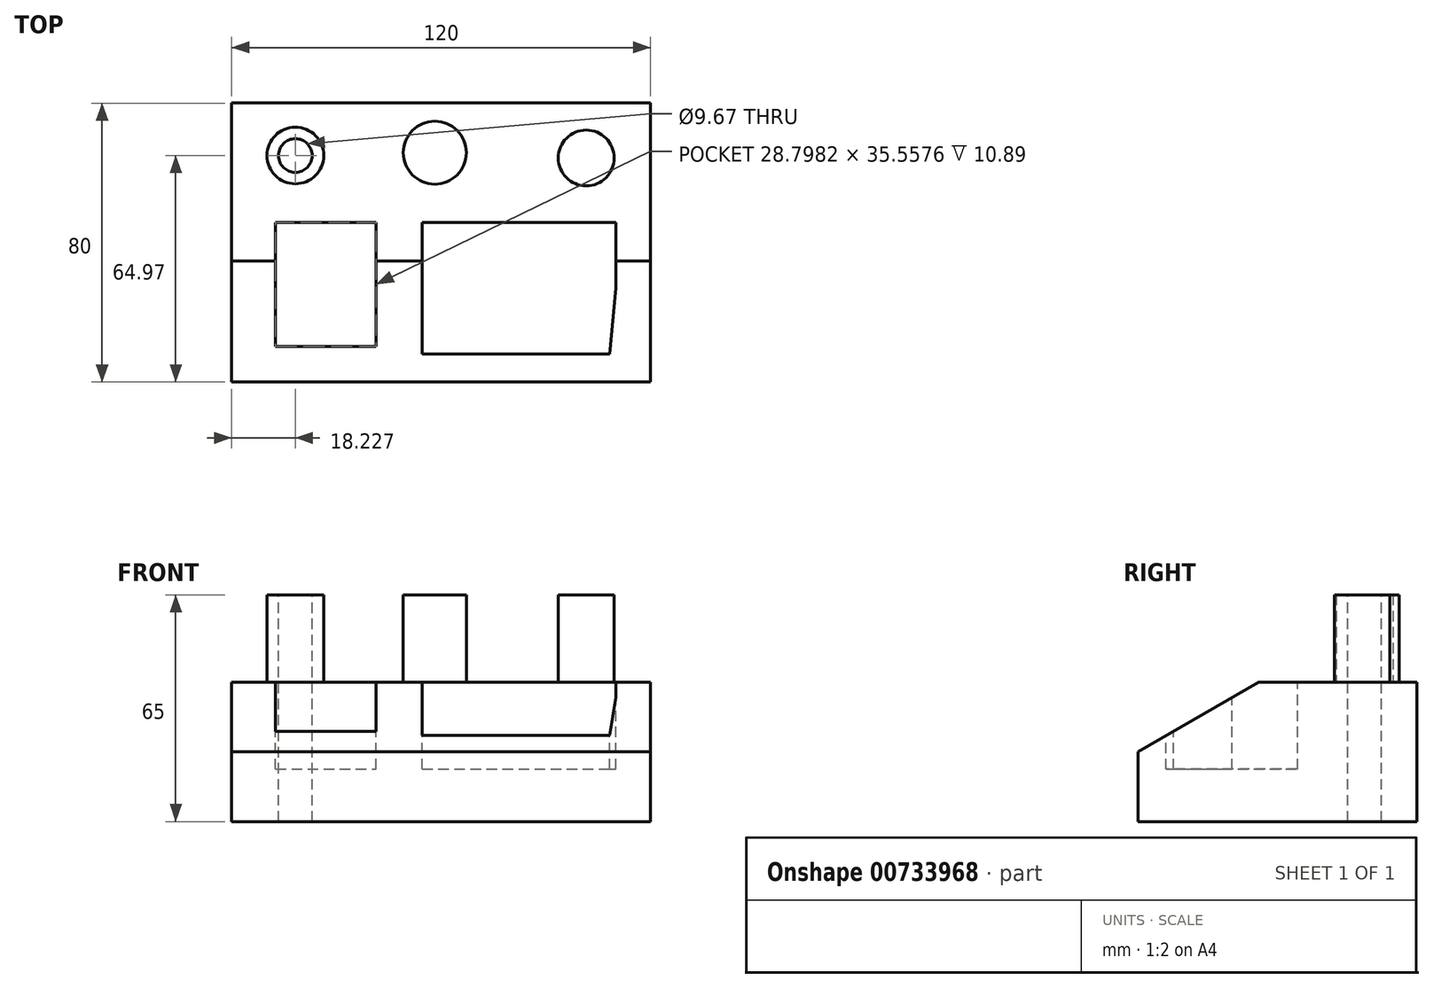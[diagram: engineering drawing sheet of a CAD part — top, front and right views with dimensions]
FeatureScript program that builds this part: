
annotation { "Feature Type Name" : "Feature", "Feature Type Description" : "" }
export const myFeature = defineFeature(function(context is Context, id is Id, definition is map)
    precondition{}
    {
        {
            var Q0;
            Q0=qCreatedBy(makeId("Top.planeOp"),FACE);
            var sketch = newSketch(context, id + "F0", { "sketchPlane" : qUnion([Q0])});
            skLineSegment(sketch, "E0.bottom", {"start": v(-64.23, 34.23) * mm, "end": v(55.77, 34.23) * mm});
            skLineSegment(sketch, "E0.top", {"start": v(-64.23, -45.77) * mm, "end": v(55.77, -45.77) * mm});
            skLineSegment(sketch, "E0.left", {"start": v(-64.23, 34.23) * mm, "end": v(-64.23, -45.77) * mm});
            skLineSegment(sketch, "E0.right", {"start": v(55.77, 34.23) * mm, "end": v(55.77, -45.77) * mm});
            skSolve(sketch);
        }
        {
            var Q0;
            Q0 = qSketchRegion(id + "F0", true);
            extrude(context, id + "F1", {"entities" : qUnion([Q0]), "depth" : 40 * mm, "offsetDistance" : 25 * mm});
        }
        {
            var Q0;
            Q0=makeQuery(id+"F1.opExtrude","CAP_FACE",FACE,{"disambiguationData":[OSD([sQuery(id+"F0.wireOp",EDGE,"E0.bottom"),sQuery(id+"F0.wireOp",EDGE,"E0.top"),sQuery(id+"F0.wireOp",EDGE,"E0.left"),sQuery(id+"F0.wireOp",EDGE,"E0.right")])],"isStart":false});
            var sketch = newSketch(context, id + "F2", { "sketchPlane" : qUnion([Q0])});
            skLineSegment(sketch, "E1.bottom", {"start": v(-51.66, -35.56) * mm, "end": v(-22.86, -35.56) * mm});
            skLineSegment(sketch, "E1.top", {"start": v(-51.66, 0) * mm, "end": v(-22.86, 0) * mm});
            skLineSegment(sketch, "E1.left", {"start": v(-51.66, -35.56) * mm, "end": v(-51.66, 0) * mm});
            skLineSegment(sketch, "E1.right", {"start": v(-22.86, -35.56) * mm, "end": v(-22.86, 0) * mm});
            skLineSegment(sketch, "E2.bottom", {"start": v(-9.64, 0) * mm, "end": v(45.77, 0) * mm});
            skLineSegment(sketch, "E2.left", {"start": v(-9.64, 0) * mm, "end": v(-9.64, -37.68) * mm});
            skLineSegment(sketch, "E2.right", {"start": v(45.77, 0) * mm, "end": v(45.77, -18.74) * mm});
            skLineSegment(sketch, "E3", {"start": v(-9.64, -37.68) * mm, "end": v(44.11, -37.68) * mm});
            skLineSegment(sketch, "E4", {"start": v(44.11, -37.68) * mm, "end": v(45.77, -18.74) * mm});
            skSolve(sketch);
        }
        {
            var Q0;
            Q0 = qSketchRegion(id + "F2", true);
            extrude(context, id + "F3", {"entities" : qUnion([Q0]), "operationType" : NewBodyOperationType.REMOVE, "oppositeDirection" : true, "depth" : 25 * mm, "offsetDistance" : 25 * mm});
        }
        {
            var Q0;
            Q0=makeQuery(id+"F1.opExtrude","SWEPT_FACE",FACE,{"disambiguationData":[OSD([sQuery(id+"F0.wireOp",EDGE,"E0.right")])]});
            var sketch = newSketch(context, id + "F4", { "sketchPlane" : qUnion([Q0])});
            skLineSegment(sketch, "E5", {"start": v(-45.77, 20) * mm, "end": v(-11.1, 40) * mm});
            skLineSegment(sketch, "E6", {"start": v(-11.1, 40) * mm, "end": v(-45.77, 40) * mm});
            skLineSegment(sketch, "E7", {"start": v(-45.77, 40) * mm, "end": v(-45.77, 20) * mm});
            skSolve(sketch);
        }
        {
            var Q0;
            Q0 = qSketchRegion(id + "F4", true);
            extrude(context, id + "F5", {"entities" : qUnion([Q0]), "operationType" : NewBodyOperationType.REMOVE, "endBound" : BoundingType.THROUGH_ALL, "oppositeDirection" : true, "depth" : 25 * mm, "offsetDistance" : 25 * mm});
        }
        {
            var Q0;
            Q0=makeQuery(id+"F1.opExtrude","CAP_FACE",FACE,{"disambiguationData":[OSD([sQuery(id+"F0.wireOp",EDGE,"E0.bottom"),sQuery(id+"F0.wireOp",EDGE,"E0.top"),sQuery(id+"F0.wireOp",EDGE,"E0.left"),sQuery(id+"F0.wireOp",EDGE,"E0.right")])],"isStart":false});
            var sketch = newSketch(context, id + "F6", { "sketchPlane" : qUnion([Q0])});
            skCircle(sketch, "E8", {"center": v(-46, 19.2) * mm, "radius": 8.12 * mm});
            skCircle(sketch, "E9", {"center": v(-6.04, 20.01) * mm, "radius": 9.03 * mm});
            skCircle(sketch, "E10", {"center": v(37.33, 18.5) * mm, "radius": 8 * mm});
            skSolve(sketch);
        }
        {
            var Q0;
            Q0 = qSketchRegion(id + "F6", true);
            extrude(context, id + "F7", {"entities" : qUnion([Q0]), "operationType" : NewBodyOperationType.ADD, "depth" : 25 * mm, "offsetDistance" : 25 * mm});
        }
        {
            var Q0;
            Q0=makeQuery(id+"F7.opExtrude","CAP_FACE",FACE,{"disambiguationData":[OSD([sQuery(id+"F6.wireOp",EDGE,"E8")])],"isStart":false});
            var sketch = newSketch(context, id + "F8", { "sketchPlane" : qUnion([Q0])});
            skCircle(sketch, "E11", {"center": v(-46, 19.2) * mm, "radius": 4.84 * mm});
            skSolve(sketch);
        }
        {
            var Q0;
            Q0 = qSketchRegion(id + "F8", true);
            extrude(context, id + "F9", {"entities" : qUnion([Q0]), "operationType" : NewBodyOperationType.REMOVE, "endBound" : BoundingType.THROUGH_ALL, "oppositeDirection" : true, "depth" : 25 * mm, "offsetDistance" : 25 * mm});
        }
    });
